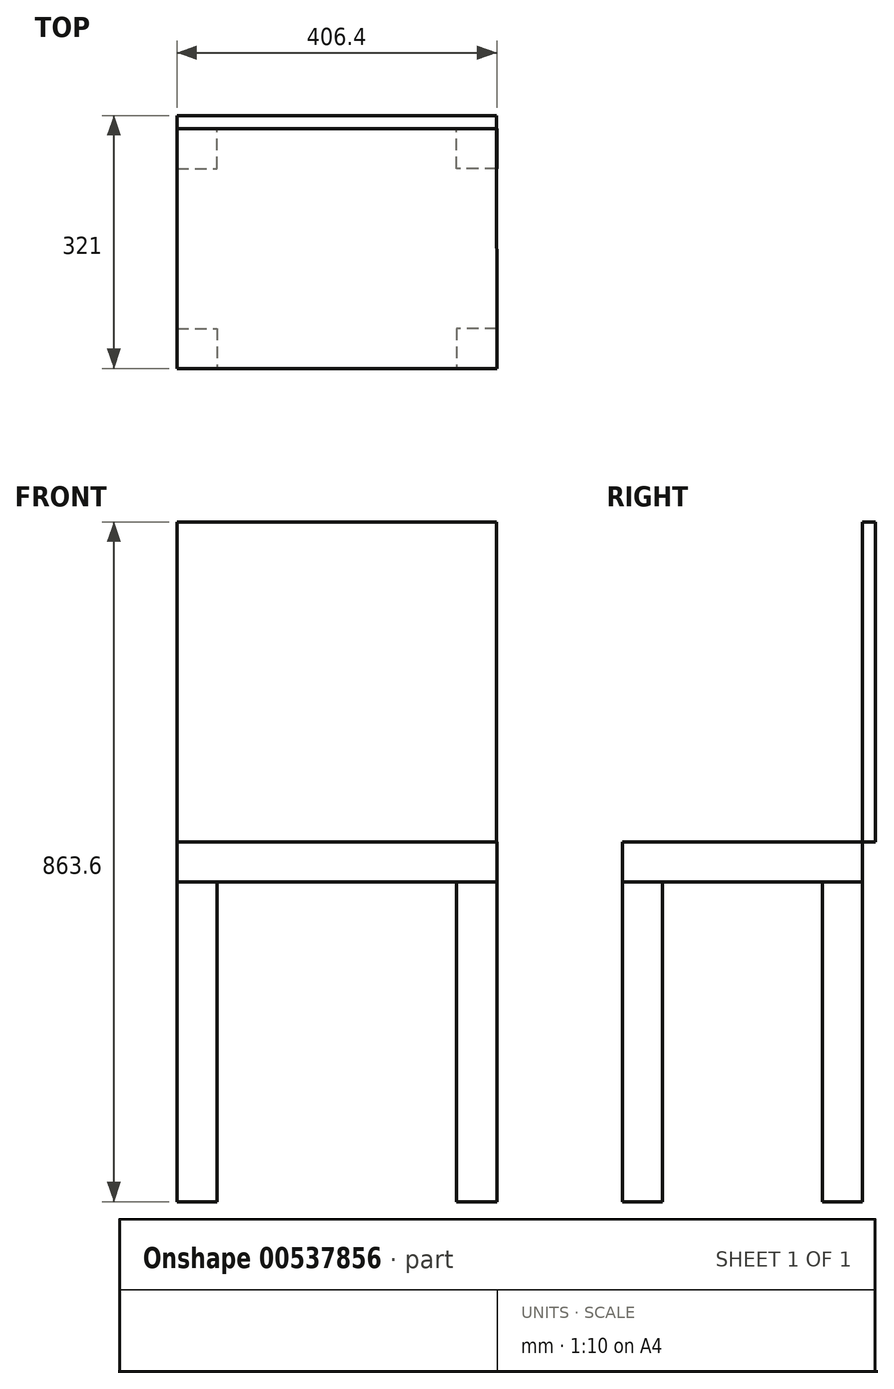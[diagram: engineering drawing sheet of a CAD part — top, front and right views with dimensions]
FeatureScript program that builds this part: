
annotation { "Feature Type Name" : "Feature", "Feature Type Description" : "" }
export const myFeature = defineFeature(function(context is Context, id is Id, definition is map)
    precondition{}
    {
        {
            var Q0;
            Q0=qCreatedBy(makeId("Top.planeOp"),FACE);
            var sketch = newSketch(context, id + "F0", { "sketchPlane" : qUnion([Q0])});
            skLineSegment(sketch, "E0", {"start": v(0, 0) * mm, "end": v(0, 50.8) * mm});
            skLineSegment(sketch, "E1", {"start": v(0, 50.8) * mm, "end": v(50.8, 50.8) * mm});
            skLineSegment(sketch, "E2", {"start": v(50.8, 50.8) * mm, "end": v(50.8, 0) * mm});
            skLineSegment(sketch, "E3", {"start": v(50.8, 0) * mm, "end": v(0, 0) * mm});
            skLineSegment(sketch, "E4", {"start": v(50.8, 12.4) * mm, "end": v(355.6, 12.4) * mm});
            skLineSegment(sketch, "E5", {"start": v(355.6, 12.4) * mm, "end": v(355.6, 0) * mm});
            skLineSegment(sketch, "E6", {"start": v(355.6, 0) * mm, "end": v(50.8, 0) * mm});
            skLineSegment(sketch, "E7", {"start": v(203.2, 0) * mm, "end": v(203.2, 304.8) * mm});
            skLineSegment(sketch, "E8", {"start": v(203.2, 152.4) * mm, "end": v(60.3, 152.4) * mm});
            skPoint(sketch, "E8.endSnap0", {"position": v(203.2, 152.4) * mm});
            skLineSegment(sketch, "E9.MirrorCS", {"start": v(0, 254) * mm, "end": v(50.8, 254) * mm});
            skLineSegment(sketch, "E10.MirrorCS", {"start": v(50.8, 254) * mm, "end": v(50.8, 304.8) * mm});
            skLineSegment(sketch, "E11.MirrorCS", {"start": v(50.8, 304.8) * mm, "end": v(0, 304.8) * mm});
            skLineSegment(sketch, "E12.MirrorCS", {"start": v(0, 304.8) * mm, "end": v(0, 254) * mm});
            skLineSegment(sketch, "E13.MirrorCS", {"start": v(355.6, 254) * mm, "end": v(355.6, 304.8) * mm});
            skLineSegment(sketch, "E14.MirrorCS", {"start": v(355.6, 304.8) * mm, "end": v(406.4, 304.8) * mm});
            skLineSegment(sketch, "E15.MirrorCS", {"start": v(406.4, 304.8) * mm, "end": v(406.4, 254) * mm});
            skLineSegment(sketch, "E16.MirrorCS", {"start": v(406.4, 254) * mm, "end": v(355.6, 254) * mm});
            skLineSegment(sketch, "E17.MirrorCS", {"start": v(406.4, 50.8) * mm, "end": v(355.6, 50.8) * mm});
            skLineSegment(sketch, "E18.MirrorCS", {"start": v(355.6, 50.8) * mm, "end": v(355.6, 0) * mm});
            skLineSegment(sketch, "E19.MirrorCS", {"start": v(355.6, 0) * mm, "end": v(406.4, 0) * mm});
            skLineSegment(sketch, "E20.MirrorCS", {"start": v(406.4, 0) * mm, "end": v(406.4, 50.8) * mm});
            skSolve(sketch);
        }
        {
            var Q0;
            Q0=makeQuery(id+"F0.imprint","IMPRINT",FACE,{"disambiguationData":[TD([[makeQuery(id+"F0.imprint","IMPRINT",EDGE,{"derivedFrom":sQuery(id+"F0.wireOp",EDGE,"E0")}),-1.0]])]});
            var Q1;
            Q1=makeQuery(id+"F0.imprint","IMPRINT",FACE,{"disambiguationData":[TD([[makeQuery(id+"F0.imprint","IMPRINT",EDGE,{"derivedFrom":sQuery(id+"F0.wireOp",EDGE,"E9.MirrorCS")}),1.0]])]});
            var Q2;
            Q2=makeQuery(id+"F0.imprint","IMPRINT",FACE,{"disambiguationData":[TD([[makeQuery(id+"F0.imprint","IMPRINT",EDGE,{"derivedFrom":sQuery(id+"F0.wireOp",EDGE,"E13.MirrorCS")}),-1.0]])]});
            var Q3;
            {var subQ3=sQuery(id+"F0.wireOp",EDGE,"E17.MirrorCS");Q3=makeQuery(id+"F0.imprint","IMPRINT",FACE,{"disambiguationData":[TD([[makeQuery(id+"F0.imprint","IMPRINT",EDGE,{"derivedFrom":subQ3}),1.0]])]});}
            extrude(context, id + "F1", {"entities" : qUnion([Q0, Q1, Q2, Q3]), "depth" : 406.4 * mm, "offsetDistance" : 25.4 * mm});
        }
        {
            var Q0;
            Q0=makeQuery(id+"F1.opExtrude","CAP_FACE",FACE,{"disambiguationData":[OSD([sQuery(id+"F0.wireOp",EDGE,"E17.MirrorCS"),sQuery(id+"F0.wireOp",EDGE,"E18.MirrorCS"),sQuery(id+"F0.wireOp",EDGE,"E19.MirrorCS"),sQuery(id+"F0.wireOp",EDGE,"E20.MirrorCS")])],"isStart":false});
            var sketch = newSketch(context, id + "F2", { "sketchPlane" : qUnion([Q0])});
            skLineSegment(sketch, "E21", {"start": v(0, 0) * mm, "end": v(0, 304.2) * mm});
            skLineSegment(sketch, "E22", {"start": v(0, 304.2) * mm, "end": v(406.16, 304.2) * mm});
            skLineSegment(sketch, "E23", {"start": v(406.16, 304.2) * mm, "end": v(406.4, 0) * mm});
            skLineSegment(sketch, "E24", {"start": v(406.4, 0) * mm, "end": v(0, 0) * mm});
            skSolve(sketch);
        }
        {
            var Q0;
            {var subQ5=makeQuery(id+"F1.opExtrude","CAP_EDGE",EDGE,{"disambiguationData":[OSD([sQuery(id+"F0.wireOp",EDGE,"E18.MirrorCS")])],"isStart":false});Q0=makeQuery(id+"F2.imprint","IMPRINT",FACE,{"disambiguationData":[TD([[makeQuery(id+"F2.imprint","IMPRINT",EDGE,{"derivedFrom":subQ5}),1.0]])]});}
            var Q1;
            {var subQ2=sQuery(id+"F2.wireOp",EDGE,"E21");Q1=makeQuery(id+"F2.imprint","IMPRINT",FACE,{"disambiguationData":[TD([[makeQuery(id+"F2.imprint","IMPRINT",EDGE,{"derivedFrom":subQ2}),-1.0]])]});}
            extrude(context, id + "F3", {"entities" : qUnion([Q0, Q1]), "depth" : 50.8 * mm, "offsetDistance" : 25.4 * mm});
        }
        {
            var Q0;
            Q0=makeQuery(id+"F3.opExtrude","CAP_FACE",FACE,{"disambiguationData":[OSD([sQuery(id+"F2.wireOp",EDGE,"E21"),sQuery(id+"F2.wireOp",EDGE,"E22"),sQuery(id+"F2.wireOp",EDGE,"E23"),sQuery(id+"F2.wireOp",EDGE,"E24")])],"isStart":false});
            var sketch = newSketch(context, id + "F4", { "sketchPlane" : qUnion([Q0])});
            skLineSegment(sketch, "E25", {"start": v(0, 304.2) * mm, "end": v(0, 321) * mm});
            skLineSegment(sketch, "E26", {"start": v(0, 321) * mm, "end": v(406.16, 321) * mm});
            skLineSegment(sketch, "E27", {"start": v(406.16, 321) * mm, "end": v(406.16, 304.2) * mm});
            skLineSegment(sketch, "E28", {"start": v(406.16, 304.2) * mm, "end": v(0, 304.2) * mm});
            skSolve(sketch);
        }
        {
            var Q0;
            Q0=makeQuery(id+"F4.imprint","IMPRINT",FACE,{"disambiguationData":[TD([[makeQuery(id+"F4.imprint","IMPRINT",EDGE,{"derivedFrom":sQuery(id+"F4.wireOp",EDGE,"E25")}),-1.0]])]});
            extrude(context, id + "F5", {"entities" : qUnion([Q0]), "depth" : 406.4 * mm, "offsetDistance" : 25.4 * mm});
        }
    });
